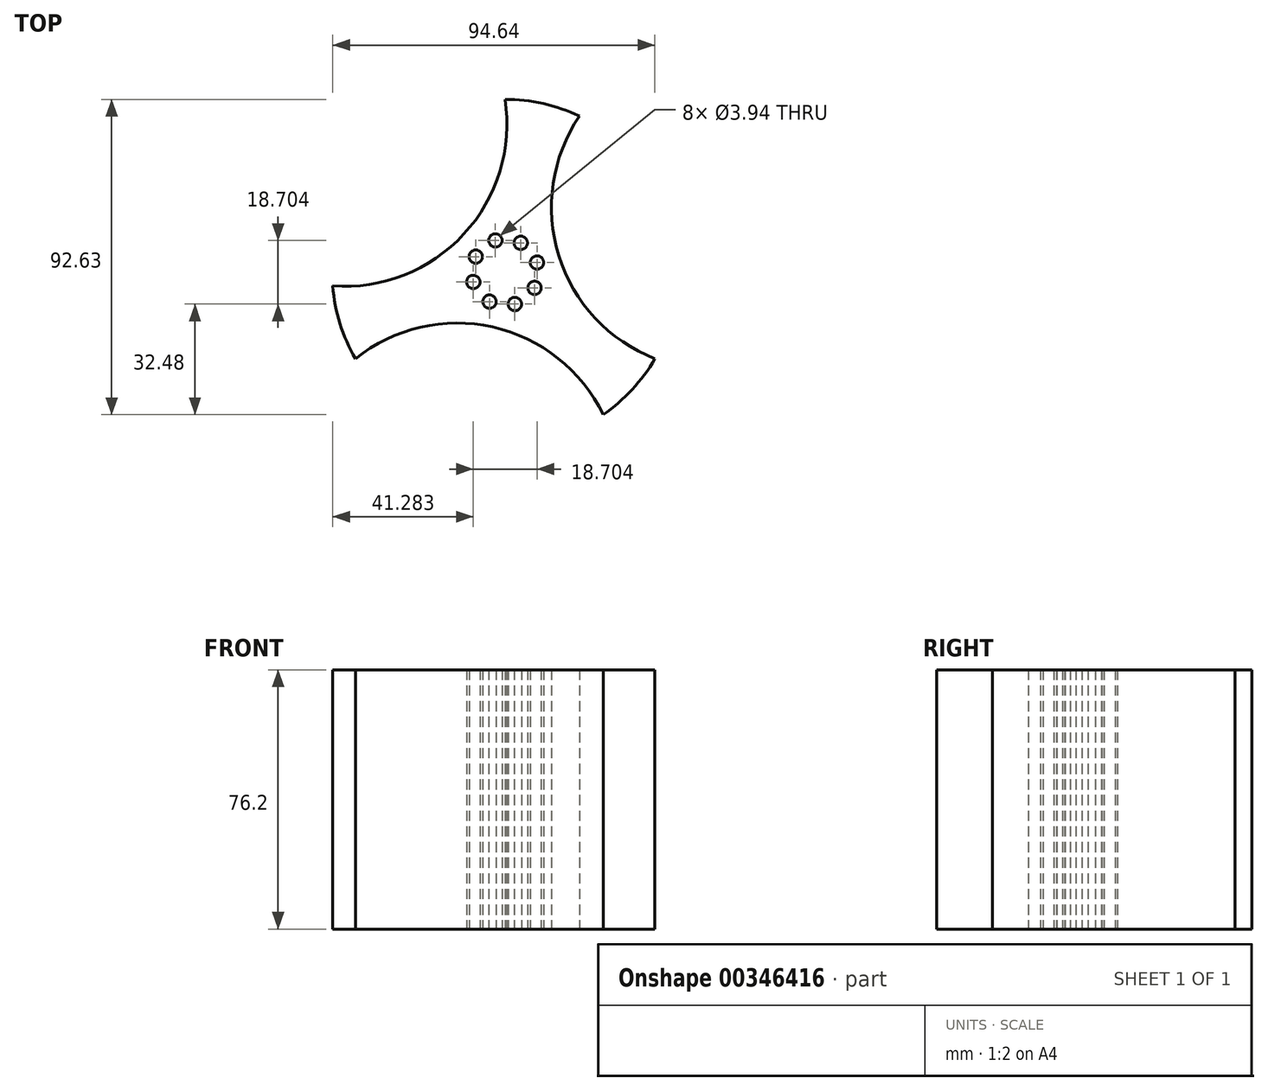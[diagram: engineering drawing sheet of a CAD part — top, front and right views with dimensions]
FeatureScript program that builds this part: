
annotation { "Feature Type Name" : "Feature", "Feature Type Description" : "" }
export const myFeature = defineFeature(function(context is Context, id is Id, definition is map)
    precondition{}
    {
        {
            var Q0;
            Q0=qCreatedBy(makeId("Top.planeOp"),FACE);
            var sketch = newSketch(context, id + "F0", { "sketchPlane" : qUnion([Q0])});
            skCircle(sketch, "E0", {"center": v(-87.06, 29.2) * mm, "radius": 16.51 * mm});
            skArc(sketch, "E1", {"start": v(-65.24, 75.07) * mm, "mid": v(-75.89, 78.75) * mm, "end": v(-87.08, 80) * mm});
            skArc(sketch, "E2", {"start": v(-58.25, -12.64) * mm, "mid": v(-49.74, -5.27) * mm, "end": v(-43.06, 3.8) * mm});
            skArc(sketch, "E3", {"start": v(-137.7, 25.15) * mm, "mid": v(-135.57, 14.1) * mm, "end": v(-131.05, 3.78) * mm});
            skArc(sketch, "E4", {"start": v(-137.7, 25.15) * mm, "mid": v(-99.2, 40.4) * mm, "end": v(-87.08, 80) * mm});
            skArc(sketch, "E5", {"start": v(-65.24, 75.07) * mm, "mid": v(-71.3, 34.1) * mm, "end": v(-43.06, 3.8) * mm});
            skArc(sketch, "E6", {"start": v(-58.25, -12.64) * mm, "mid": v(-90.7, 13.09) * mm, "end": v(-131.05, 3.78) * mm});
            skCircle(sketch, "E7", {"center": v(-87.06, 29.2) * mm, "radius": 9.78 * mm});
            skCircle(sketch, "E8", {"center": v(-82.47, 37.83) * mm, "radius": 1.97 * mm});
            skCircle(sketch, "E9.1.0", {"center": v(-89.92, 38.54) * mm, "radius": 1.97 * mm});
            skCircle(sketch, "E9.2.0", {"center": v(-95.7, 33.78) * mm, "radius": 1.97 * mm});
            skCircle(sketch, "E9.3.0", {"center": v(-96.42, 26.33) * mm, "radius": 1.97 * mm});
            skCircle(sketch, "E9.4.0", {"center": v(-91.66, 20.56) * mm, "radius": 1.97 * mm});
            skCircle(sketch, "E9.5.0", {"center": v(-84.2, 19.84) * mm, "radius": 1.97 * mm});
            skCircle(sketch, "E9.6.0", {"center": v(-78.43, 24.6) * mm, "radius": 1.97 * mm});
            skCircle(sketch, "E9.7.0", {"center": v(-77.71, 32.05) * mm, "radius": 1.97 * mm});
            skSolve(sketch);
        }
        {
            var Q0;
            Q0 = qSketchRegion(id + "F0", true);
            var Q1;
            {var subQ0=sQuery(id+"F0.wireOp",EDGE,"E9.7.0");var subQ1=sQuery(id+"F0.wireOp",EDGE,"E7");var subQ14=makeQuery(id+"F0.imprint","INTERSECT",VERTEX,{"disambiguationData":[OD(0.0)],"derivedFrom":[subQ1,subQ0]});Q1=makeQuery(id+"F0.imprint","IMPRINT",FACE,{"disambiguationData":[TD([[makeQuery(id+"F0.imprint","IMPRINT",EDGE,{"disambiguationData":[TD([[subQ14,-1.0]])],"derivedFrom":subQ1}),1.0]])]});}
            extrude(context, id + "F1", {"entities" : qUnion([Q0, Q1]), "depth" : 38.1 * mm, "hasSecondDirection" : true, "secondDirectionOppositeDirection" : true, "secondDirectionDepth" : 38.1 * mm});
        }
    });
